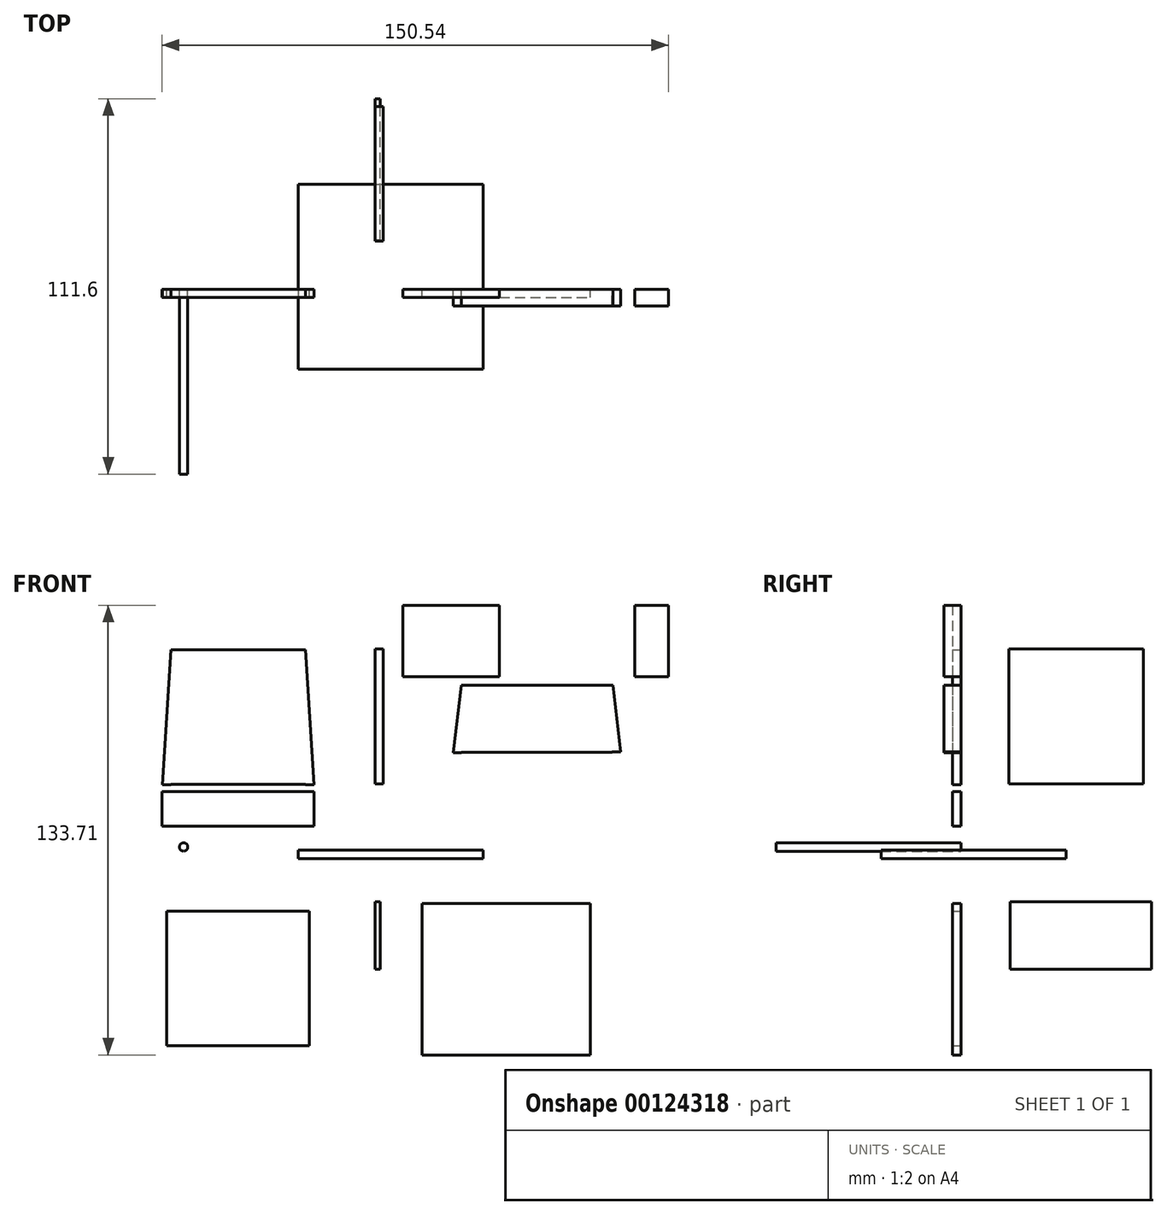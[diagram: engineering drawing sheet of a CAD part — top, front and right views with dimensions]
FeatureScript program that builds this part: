
annotation { "Feature Type Name" : "Feature", "Feature Type Description" : "" }
export const myFeature = defineFeature(function(context is Context, id is Id, definition is map)
    precondition{}
    {
        {
            var Q0;
            Q0=qCreatedBy(makeId("Top.planeOp"),FACE);
            var sketch = newSketch(context, id + "F0", { "sketchPlane" : qUnion([Q0])});
            skLineSegment(sketch, "E0.bottom", {"start": v(-22.79, 31.22) * mm, "end": v(32.21, 31.22) * mm});
            skLineSegment(sketch, "E0.top", {"start": v(-22.79, -23.78) * mm, "end": v(32.21, -23.78) * mm});
            skLineSegment(sketch, "E0.left", {"start": v(-22.79, 31.22) * mm, "end": v(-22.79, -23.78) * mm});
            skLineSegment(sketch, "E0.right", {"start": v(32.21, 31.22) * mm, "end": v(32.21, -23.78) * mm});
            skSolve(sketch);
        }
        {
            var Q0;
            Q0=makeQuery(id+"F0.imprint","IMPRINT",FACE,{"disambiguationData":[TD([[makeQuery(id+"F0.imprint","IMPRINT",EDGE,{"derivedFrom":sQuery(id+"F0.wireOp",EDGE,"E0.bottom")}),-1.0]])]});
            extrude(context, id + "F1", {"entities" : qUnion([Q0]), "depth" : 2.5 * mm});
        }
        {
            var Q0;
            Q0=qCreatedBy(makeId("Front.planeOp"),FACE);
            var sketch = newSketch(context, id + "F2", { "sketchPlane" : qUnion([Q0])});
            skLineSegment(sketch, "E1.bottom", {"start": v(-60.67, 62.02) * mm, "end": v(-20.67, 62.02) * mm});
            skLineSegment(sketch, "E1.top", {"start": v(-60.67, 22.02) * mm, "end": v(-20.67, 22.02) * mm});
            skLineSegment(sketch, "E2.top", {"start": v(-60.67, 21.9) * mm, "end": v(-63.17, 21.9) * mm});
            skLineSegment(sketch, "E2.left", {"start": v(-60.67, 22.02) * mm, "end": v(-60.67, 21.9) * mm});
            skLineSegment(sketch, "E3", {"start": v(-60.67, 62.02) * mm, "end": v(-63.17, 21.9) * mm});
            skLineSegment(sketch, "E4.top", {"start": v(-20.67, 21.9) * mm, "end": v(-18.17, 21.9) * mm});
            skLineSegment(sketch, "E4.left", {"start": v(-20.67, 22.02) * mm, "end": v(-20.67, 21.9) * mm});
            skLineSegment(sketch, "E5", {"start": v(-20.67, 62.02) * mm, "end": v(-18.17, 21.9) * mm});
            skLineSegment(sketch, "E6", {"start": v(-60.67, 62.02) * mm, "end": v(74.5, 62.02) * mm, "construction": true});
            skLineSegment(sketch, "E7", {"start": v(-103.1, 62.02) * mm, "end": v(17.88, 62.02) * mm, "construction": true});
            skSolve(sketch);
        }
        {
            var Q0;
            Q0=makeQuery(id+"F2.imprint","IMPRINT",FACE,{"disambiguationData":[TD([[makeQuery(id+"F2.imprint","IMPRINT",EDGE,{"derivedFrom":sQuery(id+"F2.wireOp",EDGE,"E1.bottom")}),-1.0]])]});
            extrude(context, id + "F3", {"entities" : qUnion([Q0]), "depth" : 2.5 * mm});
        }
        {
            var Q0;
            Q0=qCreatedBy(makeId("Right.planeOp"),FACE);
            var sketch = newSketch(context, id + "F4", { "sketchPlane" : qUnion([Q0])});
            skLineSegment(sketch, "E8.bottom", {"start": v(14.3, 62.28) * mm, "end": v(54.3, 62.28) * mm});
            skLineSegment(sketch, "E8.top", {"start": v(14.3, 22.2) * mm, "end": v(54.3, 22.2) * mm});
            skLineSegment(sketch, "E8.left", {"start": v(14.3, 62.28) * mm, "end": v(14.3, 22.2) * mm});
            skLineSegment(sketch, "E8.right", {"start": v(54.3, 62.28) * mm, "end": v(54.3, 22.2) * mm});
            skSolve(sketch);
        }
        {
            var Q0;
            Q0=makeQuery(id+"F4.imprint","IMPRINT",FACE,{"disambiguationData":[TD([[makeQuery(id+"F4.imprint","IMPRINT",EDGE,{"derivedFrom":sQuery(id+"F4.wireOp",EDGE,"E8.bottom")}),-1.0]])]});
            extrude(context, id + "F5", {"entities" : qUnion([Q0]), "depth" : 2.5 * mm});
        }
        {
            var Q0;
            Q0=qCreatedBy(makeId("Right.planeOp"),FACE);
            var sketch = newSketch(context, id + "F6", { "sketchPlane" : qUnion([Q0])});
            skLineSegment(sketch, "E9.bottom", {"start": v(14.6, -12.93) * mm, "end": v(56.6, -12.93) * mm});
            skLineSegment(sketch, "E9.top", {"start": v(14.6, -32.93) * mm, "end": v(56.6, -32.93) * mm});
            skLineSegment(sketch, "E9.left", {"start": v(14.6, -12.93) * mm, "end": v(14.6, -32.93) * mm});
            skLineSegment(sketch, "E9.right", {"start": v(56.6, -12.93) * mm, "end": v(56.6, -32.93) * mm});
            skSolve(sketch);
        }
        {
            var Q0;
            Q0 = qSketchRegion(id + "F6", true);
            extrude(context, id + "F7", {"entities" : qUnion([Q0]), "depth" : 1.5 * mm});
        }
        {
            var Q0;
            Q0=qCreatedBy(makeId("Front.planeOp"),FACE);
            var sketch = newSketch(context, id + "F8", { "sketchPlane" : qUnion([Q0])});
            skLineSegment(sketch, "E10.bottom", {"start": v(25.74, 51.59) * mm, "end": v(70.74, 51.59) * mm});
            skLineSegment(sketch, "E10.top", {"start": v(25.74, 31.59) * mm, "end": v(70.5, 31.59) * mm});
            skLineSegment(sketch, "E10.right", {"start": v(70.5, 31.74) * mm, "end": v(70.5, 31.59) * mm});
            skLineSegment(sketch, "E11.top", {"start": v(70.5, 31.74) * mm, "end": v(73, 31.74) * mm});
            skLineSegment(sketch, "E12.top", {"start": v(25.74, 31.44) * mm, "end": v(23.24, 31.44) * mm});
            skLineSegment(sketch, "E12.left", {"start": v(25.74, 31.59) * mm, "end": v(25.74, 31.44) * mm});
            skLineSegment(sketch, "E13", {"start": v(70.74, 51.59) * mm, "end": v(73, 31.74) * mm});
            skLineSegment(sketch, "E14", {"start": v(25.74, 51.59) * mm, "end": v(23.24, 31.44) * mm});
            skLineSegment(sketch, "E15", {"start": v(25.74, 51.59) * mm, "end": v(25.74, 31.59) * mm, "construction": true});
            skSolve(sketch);
        }
        {
            var Q0;
            Q0=makeQuery(id+"F8.imprint","IMPRINT",FACE,{"disambiguationData":[TD([[makeQuery(id+"F8.imprint","IMPRINT",EDGE,{"derivedFrom":sQuery(id+"F8.wireOp",EDGE,"E10.bottom")}),-1.0]])]});
            extrude(context, id + "F9", {"entities" : qUnion([Q0]), "depth" : 5 * mm});
        }
        {
            var Q0;
            Q0=qCreatedBy(makeId("Front.planeOp"),FACE);
            var sketch = newSketch(context, id + "F10", { "sketchPlane" : qUnion([Q0])});
            skLineSegment(sketch, "E16.bottom", {"start": v(-61.97, -15.6) * mm, "end": v(-19.47, -15.6) * mm});
            skLineSegment(sketch, "E16.top", {"start": v(-61.97, -55.6) * mm, "end": v(-19.47, -55.6) * mm});
            skLineSegment(sketch, "E16.left", {"start": v(-61.97, -15.6) * mm, "end": v(-61.97, -55.6) * mm});
            skLineSegment(sketch, "E16.right", {"start": v(-19.47, -15.6) * mm, "end": v(-19.47, -55.6) * mm});
            skSolve(sketch);
        }
        {
            var Q0;
            Q0 = qSketchRegion(id + "F10", true);
            extrude(context, id + "F11", {"entities" : qUnion([Q0]), "depth" : 2.5 * mm});
        }
        {
            var Q0;
            Q0=qCreatedBy(makeId("Front.planeOp"),FACE);
            var sketch = newSketch(context, id + "F12", { "sketchPlane" : qUnion([Q0])});
            skLineSegment(sketch, "E17.bottom", {"start": v(14.02, -13.4) * mm, "end": v(64.02, -13.4) * mm});
            skLineSegment(sketch, "E17.top", {"start": v(14.02, -58.4) * mm, "end": v(64.02, -58.4) * mm});
            skLineSegment(sketch, "E17.left", {"start": v(14.02, -13.4) * mm, "end": v(14.02, -58.4) * mm});
            skLineSegment(sketch, "E17.right", {"start": v(64.02, -13.4) * mm, "end": v(64.02, -58.4) * mm});
            skSolve(sketch);
        }
        {
            var Q0;
            Q0=makeQuery(id+"F12.imprint","IMPRINT",FACE,{"disambiguationData":[TD([[makeQuery(id+"F12.imprint","IMPRINT",EDGE,{"derivedFrom":sQuery(id+"F12.wireOp",EDGE,"E17.bottom")}),-1.0]])]});
            extrude(context, id + "F13", {"entities" : qUnion([Q0]), "depth" : 2.5 * mm});
        }
        {
            var Q0;
            Q0=qCreatedBy(makeId("Front.planeOp"),FACE);
            var sketch = newSketch(context, id + "F14", { "sketchPlane" : qUnion([Q0])});
            skCircle(sketch, "E18", {"center": v(-56.92, 3.43) * mm, "radius": 1.25 * mm});
            skSolve(sketch);
        }
        {
            var Q0;
            Q0 = qSketchRegion(id + "F14", true);
            extrude(context, id + "F15", {"entities" : qUnion([Q0]), "depth" : 55 * mm});
        }
        {
            var Q0;
            Q0=qCreatedBy(makeId("Front.planeOp"),FACE);
            var sketch = newSketch(context, id + "F16", { "sketchPlane" : qUnion([Q0])});
            skLineSegment(sketch, "E19.bottom", {"start": v(-63.3, 19.96) * mm, "end": v(-18.18, 19.96) * mm});
            skLineSegment(sketch, "E19.top", {"start": v(-63.3, 9.58) * mm, "end": v(-18.18, 9.58) * mm});
            skLineSegment(sketch, "E19.left", {"start": v(-63.3, 19.96) * mm, "end": v(-63.3, 9.58) * mm});
            skLineSegment(sketch, "E19.right", {"start": v(-18.18, 19.96) * mm, "end": v(-18.18, 9.58) * mm});
            skSolve(sketch);
        }
        {
            var Q0;
            Q0=makeQuery(id+"F16.imprint","IMPRINT",FACE,{"disambiguationData":[TD([[makeQuery(id+"F16.imprint","IMPRINT",EDGE,{"derivedFrom":sQuery(id+"F16.wireOp",EDGE,"E19.bottom")}),-1.0]])]});
            extrude(context, id + "F17", {"entities" : qUnion([Q0]), "depth" : 2.5 * mm});
        }
        {
            var Q0;
            Q0=qCreatedBy(makeId("Front.planeOp"),FACE);
            var sketch = newSketch(context, id + "F18", { "sketchPlane" : qUnion([Q0])});
            skLineSegment(sketch, "E20.bottom", {"start": v(8.28, 75.3) * mm, "end": v(37.03, 75.3) * mm});
            skLineSegment(sketch, "E20.top", {"start": v(8.28, 54.05) * mm, "end": v(37.03, 54.05) * mm});
            skLineSegment(sketch, "E20.left", {"start": v(8.28, 75.3) * mm, "end": v(8.28, 54.05) * mm});
            skLineSegment(sketch, "E20.right", {"start": v(37.03, 75.3) * mm, "end": v(37.03, 54.05) * mm});
            skLineSegment(sketch, "E21.bottom", {"start": v(77.25, 75.3) * mm, "end": v(87.25, 75.3) * mm});
            skLineSegment(sketch, "E21.top", {"start": v(77.25, 54.04) * mm, "end": v(87.25, 54.04) * mm});
            skLineSegment(sketch, "E21.left", {"start": v(77.25, 75.3) * mm, "end": v(77.25, 54.04) * mm});
            skLineSegment(sketch, "E21.right", {"start": v(87.25, 75.3) * mm, "end": v(87.25, 54.04) * mm});
            skSolve(sketch);
        }
        {
            var Q0;
            Q0 = qSketchRegion(id + "F18", true);
            extrude(context, id + "F19", {"entities" : qUnion([Q0]), "operationType" : NewBodyOperationType.ADD, "depth" : 2.5 * mm});
        }
        {
            var Q0;
            Q0 = qSketchRegion(id + "F18", true);
            var Q1;
            Q1=makeQuery(id+"F19.opExtrude","CAP_FACE",FACE,{"disambiguationData":[OSD([sQuery(id+"F18.wireOp",EDGE,"E21.bottom"),sQuery(id+"F18.wireOp",EDGE,"E21.top"),sQuery(id+"F18.wireOp",EDGE,"E21.left"),sQuery(id+"F18.wireOp",EDGE,"E21.right")])],"isStart":false});
            extrude(context, id + "F20", {"entities" : qUnion([Q0, Q1]), "operationType" : NewBodyOperationType.ADD, "depth" : 2.5 * mm});
        }
    });
